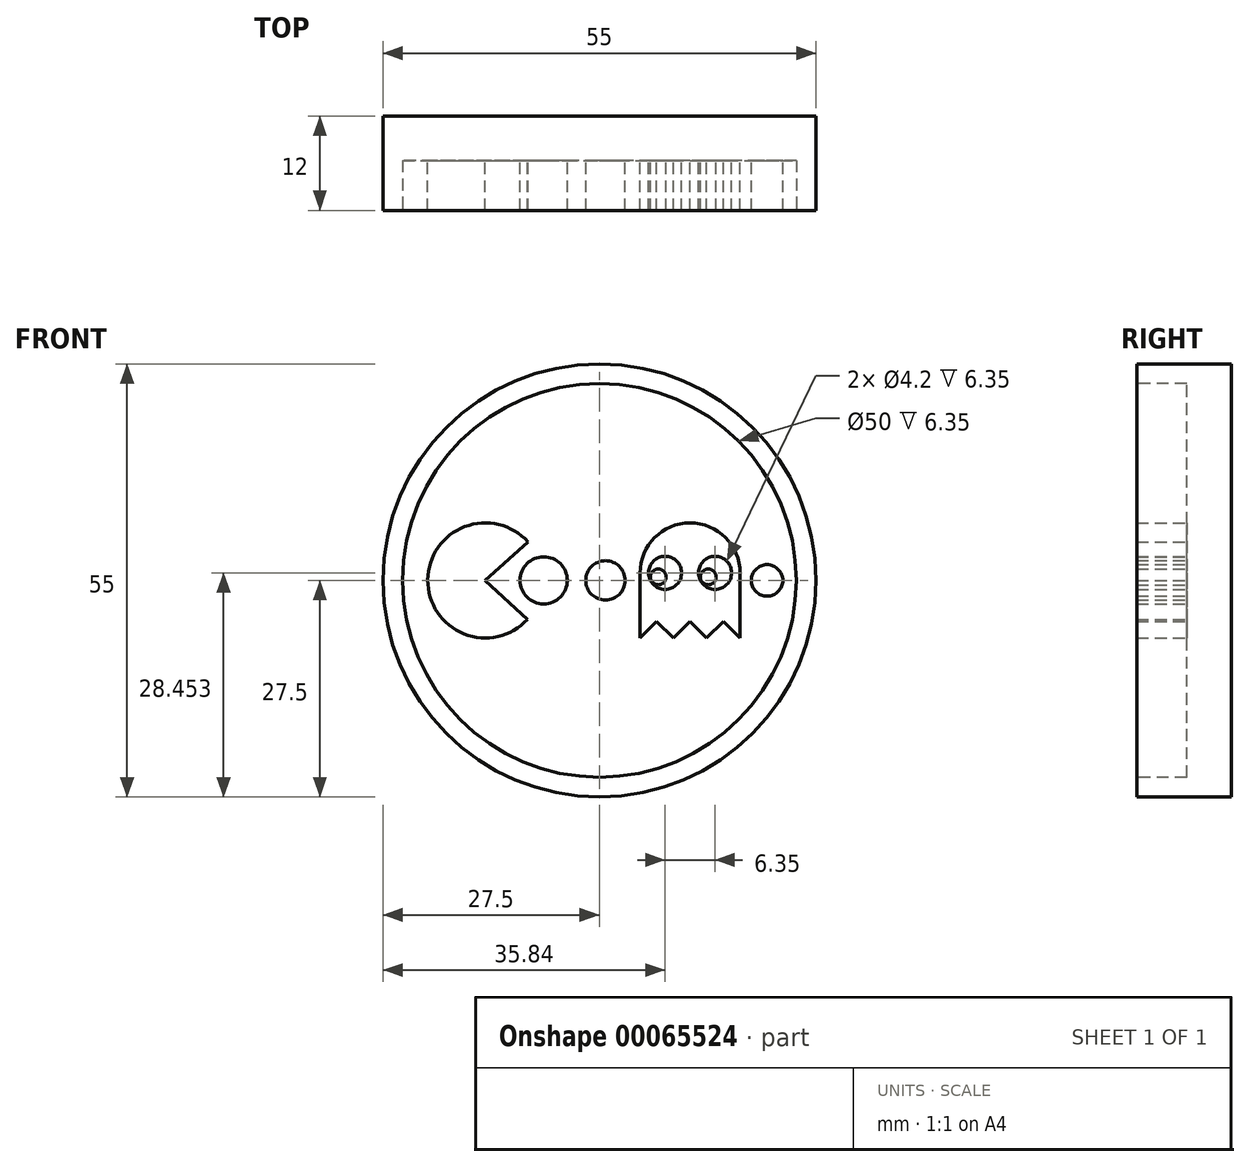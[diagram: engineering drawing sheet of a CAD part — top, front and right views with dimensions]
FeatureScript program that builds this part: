
annotation { "Feature Type Name" : "Feature", "Feature Type Description" : "" }
export const myFeature = defineFeature(function(context is Context, id is Id, definition is map)
    precondition{}
    {
        {
            var Q0;
            Q0=qCreatedBy(makeId("Front.planeOp"),FACE);
            var sketch = newSketch(context, id + "F0", { "sketchPlane" : qUnion([Q0])});
            skCircle(sketch, "E0", {"center": v(0, 0) * mm, "radius": 27.5 * mm});
            skSolve(sketch);
        }
        {
            var Q0;
            Q0=makeQuery(id+"F0.imprint","IMPRINT",FACE,{"disambiguationData":[TD([[makeQuery(id+"F0.imprint","IMPRINT",EDGE,{"derivedFrom":sQuery(id+"F0.wireOp",EDGE,"E0")}),1.0]])]});
            extrude(context, id + "F1", {"entities" : qUnion([Q0]), "depth" : 12 * mm});
        }
        {
            var Q0;
            Q0=makeQuery(id+"F1.opExtrude","CAP_FACE",FACE,{"disambiguationData":[OSD([sQuery(id+"F0.wireOp",EDGE,"E0")])],"isStart":false});
            var sketch = newSketch(context, id + "F2", { "sketchPlane" : qUnion([Q0])});
            skCircle(sketch, "E1", {"center": v(0, 0) * mm, "radius": 25 * mm});
            skSolve(sketch);
        }
        {
            var Q0;
            Q0=makeQuery(id+"F2.imprint","IMPRINT",FACE,{"disambiguationData":[TD([[makeQuery(id+"F2.imprint","IMPRINT",EDGE,{"derivedFrom":sQuery(id+"F2.wireOp",EDGE,"E1")}),1.0]])]});
            extrude(context, id + "F3", {"entities" : qUnion([Q0]), "operationType" : NewBodyOperationType.REMOVE, "oppositeDirection" : true, "depth" : 6.35 * mm});
        }
        {
            var Q0;
            Q0=makeQuery(id+"F3.boolean.opBoolean","COPY",FACE,{"derivedFrom":makeQuery(id+"F3.opExtrude","CAP_FACE",FACE,{"disambiguationData":[OSD([sQuery(id+"F2.wireOp",EDGE,"E1")])],"isStart":false})});
            var sketch = newSketch(context, id + "F4", { "sketchPlane" : qUnion([Q0])});
            skArc(sketch, "E2", {"start": v(-9.08, 4.9) * mm, "mid": v(-21.8, 0.06) * mm, "end": v(-9.16, -4.97) * mm});
            skLineSegment(sketch, "E3", {"start": v(-14.5, 0) * mm, "end": v(-9.08, 4.9) * mm});
            skLineSegment(sketch, "E4", {"start": v(-9.16, -4.97) * mm, "end": v(-14.5, 0) * mm});
            skCircle(sketch, "E5", {"center": v(-7.08, 0) * mm, "radius": 3 * mm});
            skLineSegment(sketch, "E6.left", {"start": v(5.17, 0.95) * mm, "end": v(5.17, -7.3) * mm});
            skLineSegment(sketch, "E6.right", {"start": v(17.87, 0.95) * mm, "end": v(17.87, -7.3) * mm});
            skArc(sketch, "E7", {"start": v(17.87, 0.95) * mm, "mid": v(11.52, 7.3) * mm, "end": v(5.17, 0.95) * mm});
            skLineSegment(sketch, "E8", {"start": v(5.17, -7.3) * mm, "end": v(17.87, -7.3) * mm, "construction": true});
            skLineSegment(sketch, "E9", {"start": v(5.17, 0.95) * mm, "end": v(11.52, 0.95) * mm, "construction": true});
            skCircle(sketch, "E10", {"center": v(8.34, 0.95) * mm, "radius": 2.1 * mm});
            skLineSegment(sketch, "E11", {"start": v(11.52, 0.95) * mm, "end": v(17.87, 0.95) * mm, "construction": true});
            skCircle(sketch, "E12", {"center": v(14.7, 0.95) * mm, "radius": 2.1 * mm});
            skCircle(sketch, "E13", {"center": v(7.48, 0.44) * mm, "radius": 1 * mm});
            skCircle(sketch, "E14", {"center": v(13.83, 0.44) * mm, "radius": 1 * mm});
            skCircle(sketch, "E15", {"center": v(0.77, 0) * mm, "radius": 2.5 * mm});
            skCircle(sketch, "E16", {"center": v(21.3, 0) * mm, "radius": 2 * mm});
            skLineSegment(sketch, "E17", {"start": v(11.52, -5.19) * mm, "end": v(9.4, -7.3) * mm});
            skLineSegment(sketch, "E18", {"start": v(9.4, -7.3) * mm, "end": v(7.28, -5.19) * mm});
            skLineSegment(sketch, "E19", {"start": v(7.28, -5.19) * mm, "end": v(5.17, -7.3) * mm});
            skLineSegment(sketch, "E20", {"start": v(11.52, -5.19) * mm, "end": v(13.63, -7.3) * mm});
            skLineSegment(sketch, "E21", {"start": v(13.63, -7.3) * mm, "end": v(15.75, -5.19) * mm});
            skLineSegment(sketch, "E22", {"start": v(15.75, -5.19) * mm, "end": v(17.87, -7.3) * mm});
            skCircle(sketch, "E23", {"center": v(0, 0) * mm, "radius": 25 * mm, "construction": true});
            skLineSegment(sketch, "E24", {"start": v(-25, 0) * mm, "end": v(25, 0) * mm, "construction": true});
            skSolve(sketch);
        }
        {
            var Q0;
            Q0 = qSketchRegion(id + "F4", true);
            var Q1;
            Q1=makeQuery(id+"F4.imprint","IMPRINT",FACE,{"disambiguationData":[TD([[makeQuery(id+"F4.imprint","IMPRINT",EDGE,{"derivedFrom":sQuery(id+"F4.wireOp",EDGE,"E13")}),1.0]])]});
            var Q2;
            Q2=makeQuery(id+"F4.imprint","IMPRINT",FACE,{"disambiguationData":[TD([[makeQuery(id+"F4.imprint","IMPRINT",EDGE,{"derivedFrom":sQuery(id+"F4.wireOp",EDGE,"E14")}),1.0]])]});
            extrude(context, id + "F5", {"entities" : qUnion([Q0, Q1, Q2]), "operationType" : NewBodyOperationType.ADD, "depth" : 6.35 * mm});
        }
    });
